# Revit family: Marley_Alutec_Traditional_102x76_Rectangular_Downpipe
name_source: partatom
category: Plumbing Fixtures
revit_build: Autodesk Revit 2013 (Build: 20130531_2115(x64)
units: mm (PartAtom-declared; Revit-internal decimal feet)

## types (1)
- 102x76mm
    Assembly Code = D2040
    Available Colours = http://www.marleyalutec.co.uk
    Default Elevation = 1219 mm
    Description = Traditional Rectangle 102x76mm Downpipe
    ExpectedLife = 50
    Inner Rad = 29 mm  [stored 0.0951444 ft]
    Keynote = R10/350
    Manufacturer = Marley Alutec
    Model = Traditional Rectangle 102x76mm Downpipe
    ModelNumber = RSR311 (1m) RSR312 (2m) RSR313 (3m)
    Name = Traditional Rectangle 102x76mm Downpipe
    Outter Rad = 32 mm
    Product Code = RSR311 (1m) RSR312 (2m) RSR313 (3m)
    Size = 102x76
    Type Comments = Traditional Rectangle 102x76mm Downpipe
    TypeName = Traditional Rectangle 102x76mm Downpipe
    URL = http://www.marleyalutec.co.uk
    Uniclass2 = Ss-50-30-02-28
    _BIMspec_GUID = 0
    _current revision = 1
    _distributed by = www.bimstore.co.uk

note: [stored X ft] marks values corroborated as IEEE doubles in the binary element streams (Revit-internal decimal feet)

## geometry (parser evidence)
native form markers: Blend x8, Sweep x3
no freeform markers — native parametric forms only
